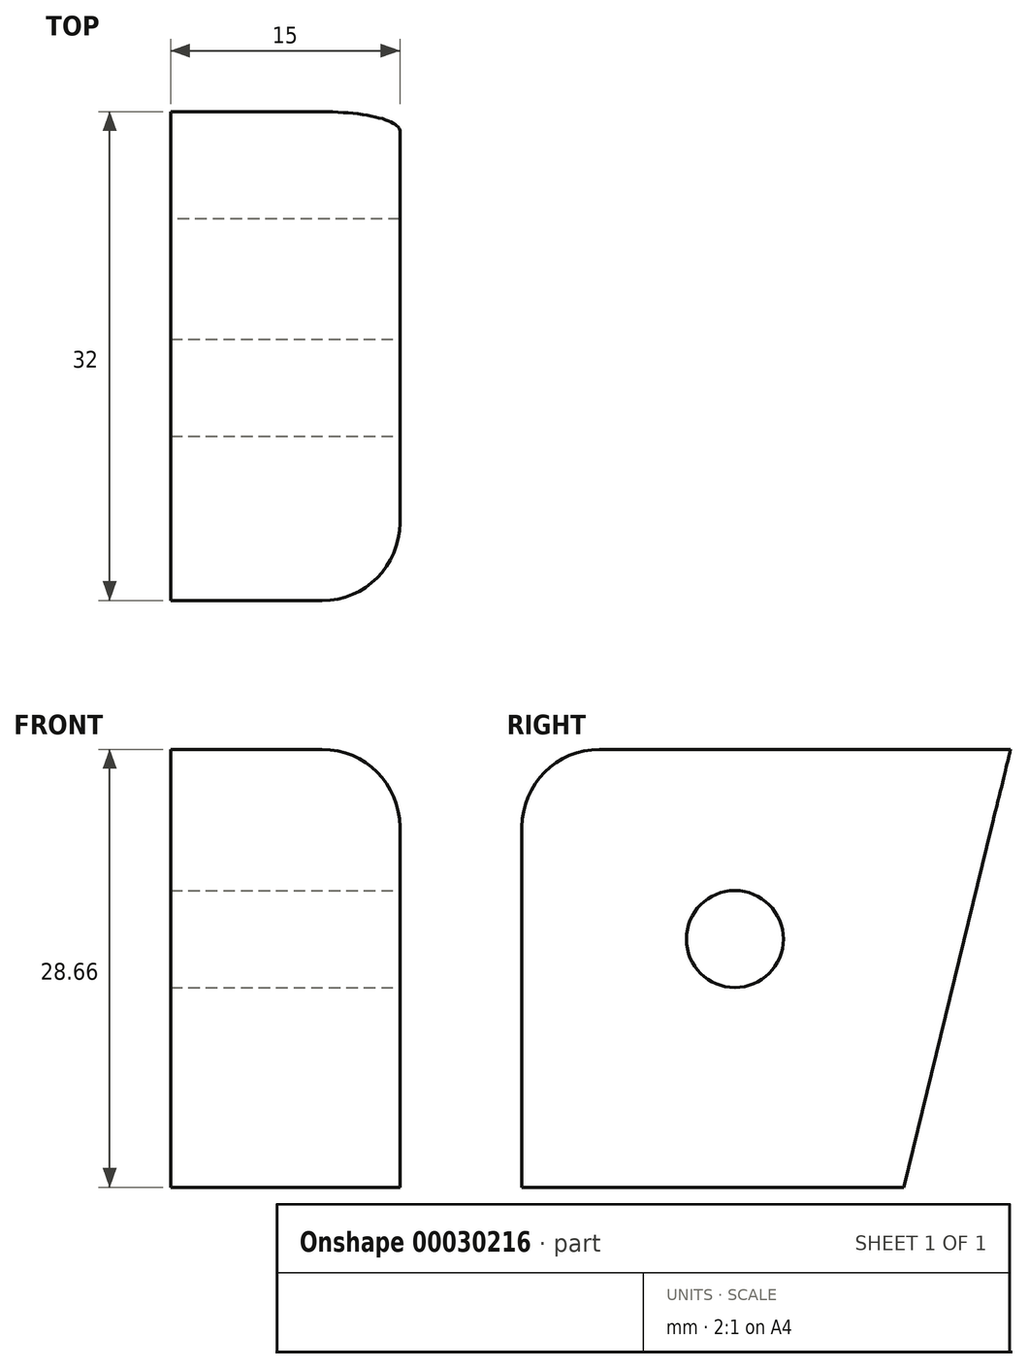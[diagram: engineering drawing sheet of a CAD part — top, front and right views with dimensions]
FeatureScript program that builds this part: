
annotation { "Feature Type Name" : "Feature", "Feature Type Description" : "" }
export const myFeature = defineFeature(function(context is Context, id is Id, definition is map)
    precondition{}
    {
        {
            var Q0;
            Q0=qCreatedBy(makeId("Right.planeOp"),FACE);
            var sketch = newSketch(context, id + "F0", { "sketchPlane" : qUnion([Q0])});
            skLineSegment(sketch, "E0.bottom", {"start": v(-21.37, 24.5) * mm, "end": v(10.63, 24.5) * mm});
            skLineSegment(sketch, "E0.top", {"start": v(-21.37, -4.17) * mm, "end": v(3.63, -4.17) * mm});
            skLineSegment(sketch, "E0.left", {"start": v(-21.37, 24.5) * mm, "end": v(-21.37, -4.17) * mm});
            skLineSegment(sketch, "E0.right", {"start": v(10.63, 24.5) * mm, "end": v(3.63, -4.17) * mm});
            skSolve(sketch);
        }
        {
            var Q0;
            Q0 = qSketchRegion(id + "F0", true);
            extrude(context, id + "F1", {"entities" : qUnion([Q0]), "depth" : 15 * mm});
        }
        {
            var Q0;
            Q0=makeQuery(id+"F1.opExtrude","CAP_EDGE",EDGE,{"disambiguationData":[OSD([sQuery(id+"F0.wireOp",EDGE,"E0.left")])],"isStart":false});
            var Q1;
            Q1=makeQuery(id+"F1.opExtrude","CAP_EDGE",EDGE,{"disambiguationData":[OSD([sQuery(id+"F0.wireOp",EDGE,"E0.bottom")])],"isStart":false});
            var Q2;
            Q2=makeQuery(id+"F1.opExtrude","SWEPT_EDGE",EDGE,{"disambiguationData":[OSD([sQuery(id+"F0.wireOp",EDGE,"E0.bottom"),sQuery(id+"F0.wireOp",EDGE,"E0.left")])]});
            fillet(context, id + "F2", {"entities" : qUnion([Q0, Q1, Q2]), "radius" : 5.08 * mm, "tangentPropagation" : true, "allowEdgeOverflow" : false});
        }
        {
            var Q0;
            Q0=makeQuery(id+"F1.opExtrude","CAP_FACE",FACE,{"disambiguationData":[OSD([sQuery(id+"F0.wireOp",EDGE,"E0.bottom"),sQuery(id+"F0.wireOp",EDGE,"E0.top"),sQuery(id+"F0.wireOp",EDGE,"E0.left"),sQuery(id+"F0.wireOp",EDGE,"E0.right")])],"isStart":false});
            var sketch = newSketch(context, id + "F3", { "sketchPlane" : qUnion([Q0])});
            skPoint(sketch, "E1", {"position": v(-7.43, 12.08) * mm});
            skSolve(sketch);
        }
        {
            var Q0;
            Q0=sQuery(id+"F3.wireOp",VERTEX,"E1");
            var Q1;
            Q1=makeQuery(id+"F1.opExtrude","SWEPT_BODY",BODY,{"disambiguationData":[OSD([sQuery(id+"F0.wireOp",EDGE,"E0.bottom"),sQuery(id+"F0.wireOp",EDGE,"E0.top"),sQuery(id+"F0.wireOp",EDGE,"E0.left"),sQuery(id+"F0.wireOp",EDGE,"E0.right")])]});
            hole(context, id + "F4", {"style" : HoleStyle.SIMPLE, "holeDiameter" : 6.35 * mm, "endStyle" : HoleEndStyle.THROUGH, "locations" : qUnion([Q0]), "scope" : qUnion([Q1])});
        }
    });
